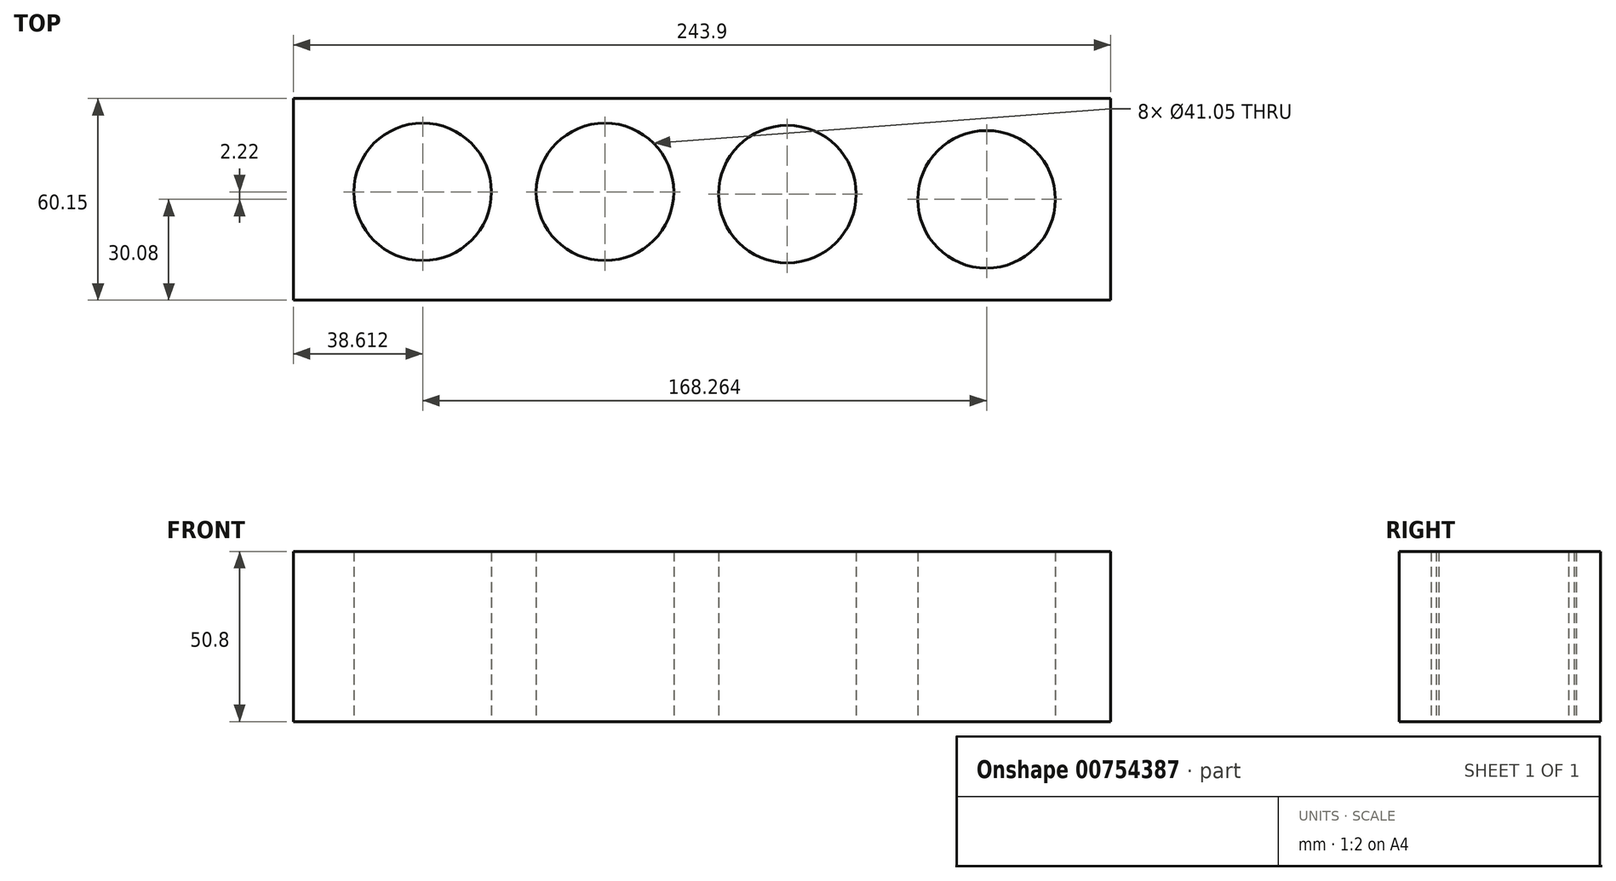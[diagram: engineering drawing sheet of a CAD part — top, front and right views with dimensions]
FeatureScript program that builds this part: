
annotation { "Feature Type Name" : "Feature", "Feature Type Description" : "" }
export const myFeature = defineFeature(function(context is Context, id is Id, definition is map)
    precondition{}
    {
        {
            var Q0;
            Q0=qCreatedBy(makeId("Top.planeOp"),FACE);
            var sketch = newSketch(context, id + "F0", { "sketchPlane" : qUnion([Q0])});
            skCircle(sketch, "E0", {"center": v(-54.4, 0) * mm, "radius": 20.53 * mm});
            skCircle(sketch, "E1", {"center": v(54.42, -0.66) * mm, "radius": 20.53 * mm});
            skCircle(sketch, "E2", {"center": v(113.87, -2.22) * mm, "radius": 20.53 * mm});
            skCircle(sketch, "E3", {"center": v(0, 0) * mm, "radius": 20.53 * mm});
            skLineSegment(sketch, "E4.bottom", {"start": v(-93, 27.85) * mm, "end": v(150.89, 27.85) * mm});
            skLineSegment(sketch, "E4.top", {"start": v(-93, -32.3) * mm, "end": v(150.89, -32.3) * mm});
            skLineSegment(sketch, "E4.left", {"start": v(-93, 27.85) * mm, "end": v(-93, -32.3) * mm});
            skLineSegment(sketch, "E4.right", {"start": v(150.89, 27.85) * mm, "end": v(150.89, -32.3) * mm});
            skLineSegment(sketch, "E5.bottom", {"start": v(150.89, -32.3) * mm, "end": v(150.89, -32.3) * mm});
            skLineSegment(sketch, "E5.top", {"start": v(150.89, -2.23) * mm, "end": v(150.89, -2.23) * mm});
            skLineSegment(sketch, "E5.left", {"start": v(150.89, -32.3) * mm, "end": v(150.89, -2.23) * mm});
            skLineSegment(sketch, "E5.right", {"start": v(150.89, -32.3) * mm, "end": v(150.89, -2.23) * mm});
            skSolve(sketch);
        }
        {
            var Q0;
            Q0=makeQuery(id+"F0.imprint","IMPRINT",FACE,{"disambiguationData":[TD([[makeQuery(id+"F0.imprint","IMPRINT",EDGE,{"derivedFrom":sQuery(id+"F0.wireOp",EDGE,"E0")}),-1.0]])]});
            extrude(context, id + "F1", {"entities" : qUnion([Q0]), "depth" : 50.8 * mm, "offsetDistance" : 25.4 * mm});
        }
    });
